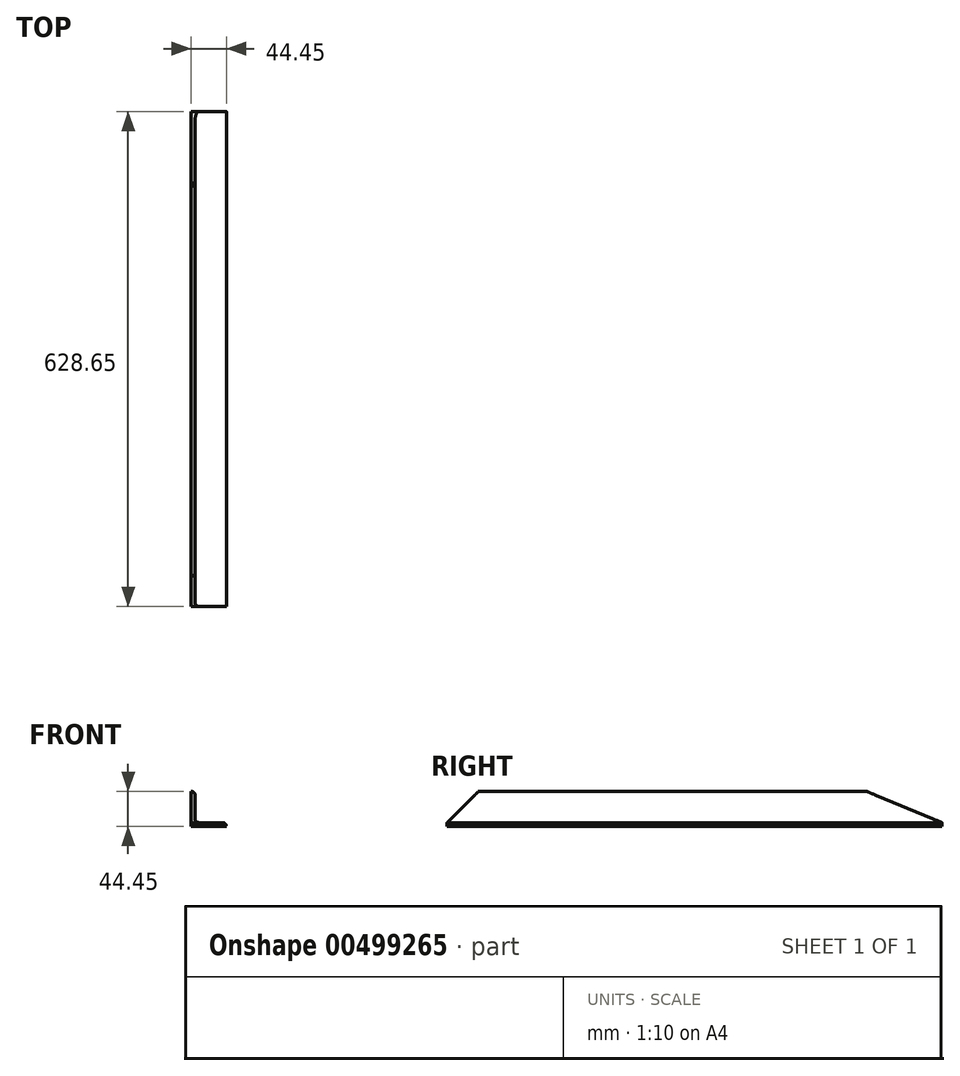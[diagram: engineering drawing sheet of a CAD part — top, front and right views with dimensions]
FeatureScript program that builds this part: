
annotation { "Feature Type Name" : "Feature", "Feature Type Description" : "" }
export const myFeature = defineFeature(function(context is Context, id is Id, definition is map)
    precondition{}
    {
        {
            var Q0;
            Q0=qCreatedBy(makeId("Front.planeOp"),FACE);
            var sketch = newSketch(context, id + "F0", { "sketchPlane" : qUnion([Q0])});
            skLineSegment(sketch, "E0", {"start": v(0, 0) * mm, "end": v(0, 44.45) * mm});
            skLineSegment(sketch, "E1", {"start": v(0, 0) * mm, "end": v(44.45, 0) * mm});
            skLineSegment(sketch, "E2", {"start": v(44.45, 0) * mm, "end": v(44.45, 4.76) * mm});
            skLineSegment(sketch, "E3", {"start": v(0, 44.45) * mm, "end": v(4.76, 44.45) * mm});
            skLineSegment(sketch, "E4", {"start": v(4.76, 44.45) * mm, "end": v(4.76, 4.76) * mm});
            skLineSegment(sketch, "E5", {"start": v(4.76, 4.76) * mm, "end": v(44.45, 4.76) * mm});
            skSolve(sketch);
        }
        {
            var Q0;
            Q0 = qSketchRegion(id + "F0", true);
            extrude(context, id + "F1", {"entities" : qUnion([Q0]), "depth" : 628.65 * mm});
        }
        {
            var Q0;
            Q0=makeQuery(id+"F1.opExtrude","SWEPT_EDGE",EDGE,{"disambiguationData":[OSD([sQuery(id+"F0.wireOp",EDGE,"E4"),sQuery(id+"F0.wireOp",EDGE,"E5")])]});
            var Q1;
            Q1=makeQuery(id+"F1.opExtrude","SWEPT_EDGE",EDGE,{"disambiguationData":[OSD([sQuery(id+"F0.wireOp",EDGE,"E3"),sQuery(id+"F0.wireOp",EDGE,"E4")])]});
            var Q2;
            Q2=makeQuery(id+"F1.opExtrude","SWEPT_EDGE",EDGE,{"disambiguationData":[OSD([sQuery(id+"F0.wireOp",EDGE,"E2"),sQuery(id+"F0.wireOp",EDGE,"E5")])]});
            fillet(context, id + "F2", {"entities" : qUnion([Q0, Q1, Q2]), "radius" : 4.76 * mm, "tangentPropagation" : true, "allowEdgeOverflow" : false});
        }
        {
            var Q0;
            Q0=makeQuery(id+"F1.opExtrude","SWEPT_FACE",FACE,{"disambiguationData":[OSD([sQuery(id+"F0.wireOp",EDGE,"E0")])]});
            var sketch = newSketch(context, id + "F3", { "sketchPlane" : qUnion([Q0])});
            skPoint(sketch, "E6.0", {"position": v(0, 4.76) * mm});
            skPoint(sketch, "E7.0", {"position": v(628.65, 4.76) * mm});
            skLineSegment(sketch, "E8", {"start": v(0, 4.76) * mm, "end": v(69.68, 4.76) * mm});
            skLineSegment(sketch, "E9", {"start": v(0, 4.76) * mm, "end": v(187.33, 82.36) * mm});
            skLineSegment(sketch, "E10", {"start": v(628.65, 4.76) * mm, "end": v(567.9, 4.76) * mm});
            skLineSegment(sketch, "E11", {"start": v(628.65, 4.76) * mm, "end": v(529.9, 103.5) * mm});
            skSolve(sketch);
        }
        {
            var Q0;
            Q0 = qSketchRegion(id + "F3", true);
            var Q1;
            {var subQ0=sQuery(id+"F3.wireOp",EDGE,"E9");var subQ1=sQuery(id+"F0.wireOp",EDGE,"E0");var subQ2=makeQuery(id+"F1.opExtrude","CAP_EDGE",EDGE,{"disambiguationData":[OSD([subQ1])],"isStart":true});var subQ3=makeQuery(id+"F3.imprint","INTERSECT",VERTEX,{"derivedFrom":[subQ2,subQ0]});Q1=makeQuery(id+"F3.imprint","IMPRINT",FACE,{"disambiguationData":[TD([[makeQuery(id+"F3.imprint","IMPRINT",EDGE,{"disambiguationData":[TD([[subQ3,-1.0]])],"derivedFrom":subQ0}),1.0]])]});}
            var Q2;
            {var subQ0=sQuery(id+"F3.wireOp",EDGE,"E11");var subQ1=sQuery(id+"F0.wireOp",EDGE,"E0");var subQ2=makeQuery(id+"F1.opExtrude","CAP_EDGE",EDGE,{"disambiguationData":[OSD([subQ1])],"isStart":false});var subQ3=makeQuery(id+"F3.imprint","INTERSECT",VERTEX,{"derivedFrom":[subQ2,subQ0]});Q2=makeQuery(id+"F3.imprint","IMPRINT",FACE,{"disambiguationData":[TD([[makeQuery(id+"F3.imprint","IMPRINT",EDGE,{"disambiguationData":[TD([[subQ3,-1.0]])],"derivedFrom":subQ0}),-1.0]])]});}
            extrude(context, id + "F4", {"entities" : qUnion([Q0, Q1, Q2]), "operationType" : NewBodyOperationType.REMOVE, "oppositeDirection" : true, "depth" : 25.4 * mm});
        }
    });
